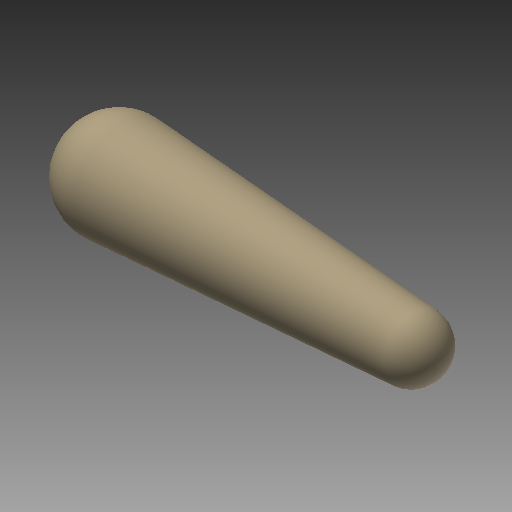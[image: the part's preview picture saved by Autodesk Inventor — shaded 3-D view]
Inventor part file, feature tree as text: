
AUTODESK INVENTOR PART (.ipt)
format: ipt  version: 2022 (Build 260153000, 153)  size: 166,912 bytes
history: native  units: mm (DEFAULTED — no unit token found)
features: other x1, revolve x1, sketch x1
ambient origin geometry x8: Origin, YZ Plane, XZ Plane, XY Plane, X Axis, Y Axis, Z Axis, Center Point
bodies: Solid1 (feature_tree)
feature tree (3):
  other  "iMan - 2D BODY"
  revolve  "Revolution1"  [1 undecoded]
  sketch  "Sketch1"  dims[d1=10.0mm d16=260.096mm d17=88.138mm d18=55.372mm d19=90.0deg]
note: 1 required parameter value undecoded (feature->parameter linkage not recoverable at this tier; creation-order binding heuristic only, values carry confidence <= 0.55)
